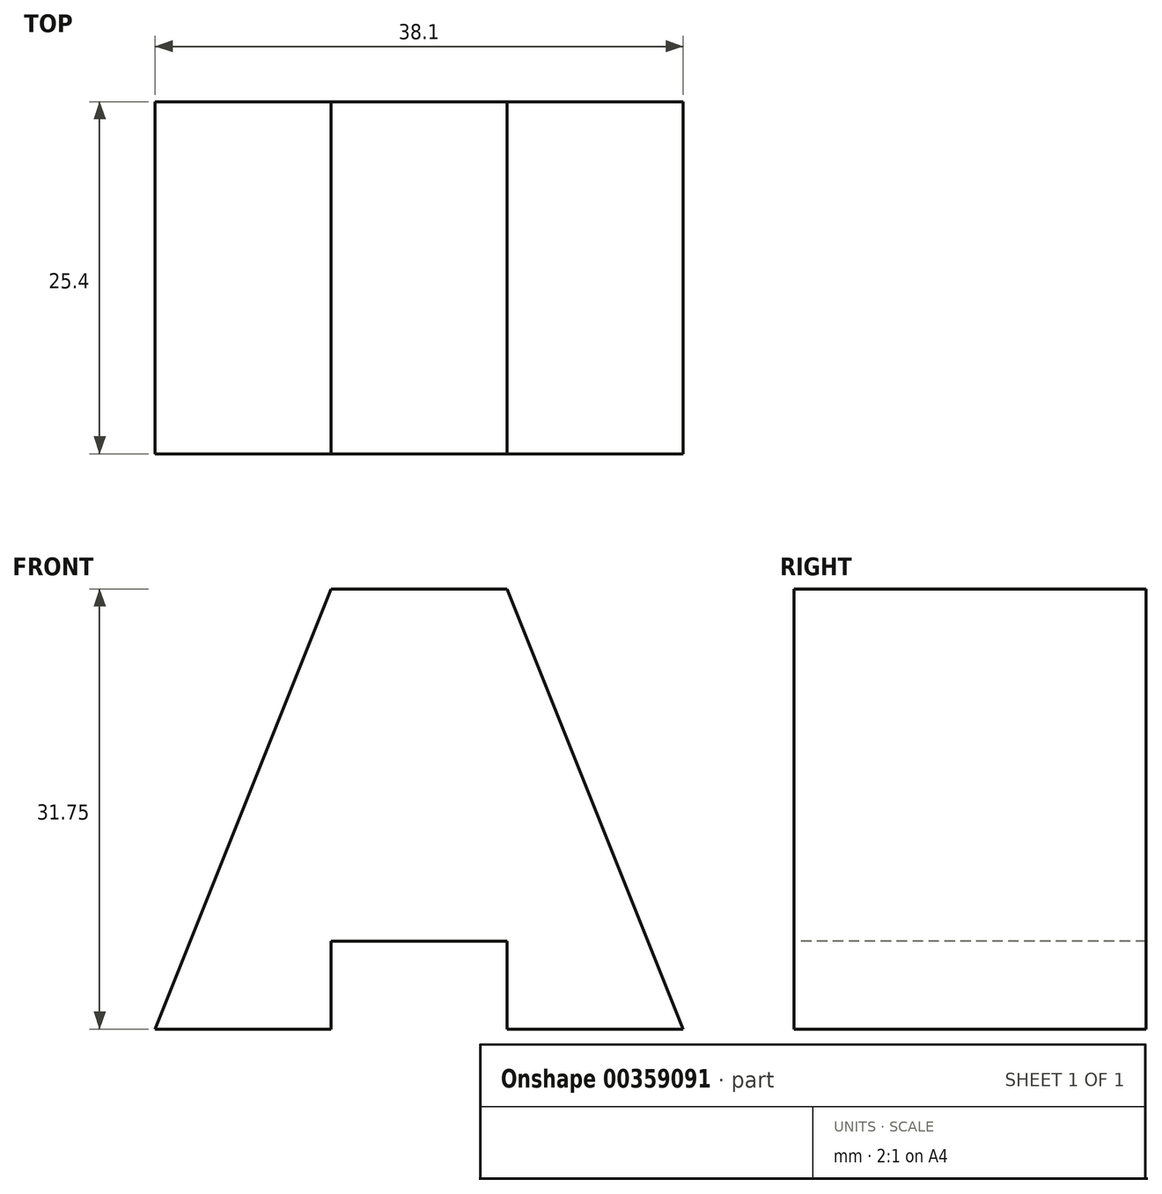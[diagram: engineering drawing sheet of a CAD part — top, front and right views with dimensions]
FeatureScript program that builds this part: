
annotation { "Feature Type Name" : "Feature", "Feature Type Description" : "" }
export const myFeature = defineFeature(function(context is Context, id is Id, definition is map)
    precondition{}
    {
        {
            var Q0;
            Q0=qCreatedBy(makeId("Front.planeOp"),FACE);
            var sketch = newSketch(context, id + "F0", { "sketchPlane" : qUnion([Q0])});
            skLineSegment(sketch, "E0", {"start": v(0, 0) * mm, "end": v(12.7, 31.75) * mm});
            skLineSegment(sketch, "E1", {"start": v(12.7, 31.75) * mm, "end": v(25.4, 31.75) * mm});
            skLineSegment(sketch, "E2", {"start": v(25.4, 31.75) * mm, "end": v(38.1, 0) * mm});
            skLineSegment(sketch, "E3", {"start": v(38.1, 0) * mm, "end": v(25.4, 0) * mm});
            skLineSegment(sketch, "E4", {"start": v(25.4, 0) * mm, "end": v(25.4, 6.35) * mm});
            skLineSegment(sketch, "E5", {"start": v(25.4, 6.35) * mm, "end": v(12.7, 6.35) * mm});
            skLineSegment(sketch, "E6", {"start": v(12.7, 6.35) * mm, "end": v(12.7, 0) * mm});
            skLineSegment(sketch, "E7", {"start": v(12.7, 0) * mm, "end": v(0, 0) * mm});
            skSolve(sketch);
        }
        {
            var Q0;
            Q0 = qSketchRegion(id + "F0", true);
            extrude(context, id + "F1", {"entities" : qUnion([Q0]), "oppositeDirection" : true, "depth" : 25.4 * mm});
        }
    });
